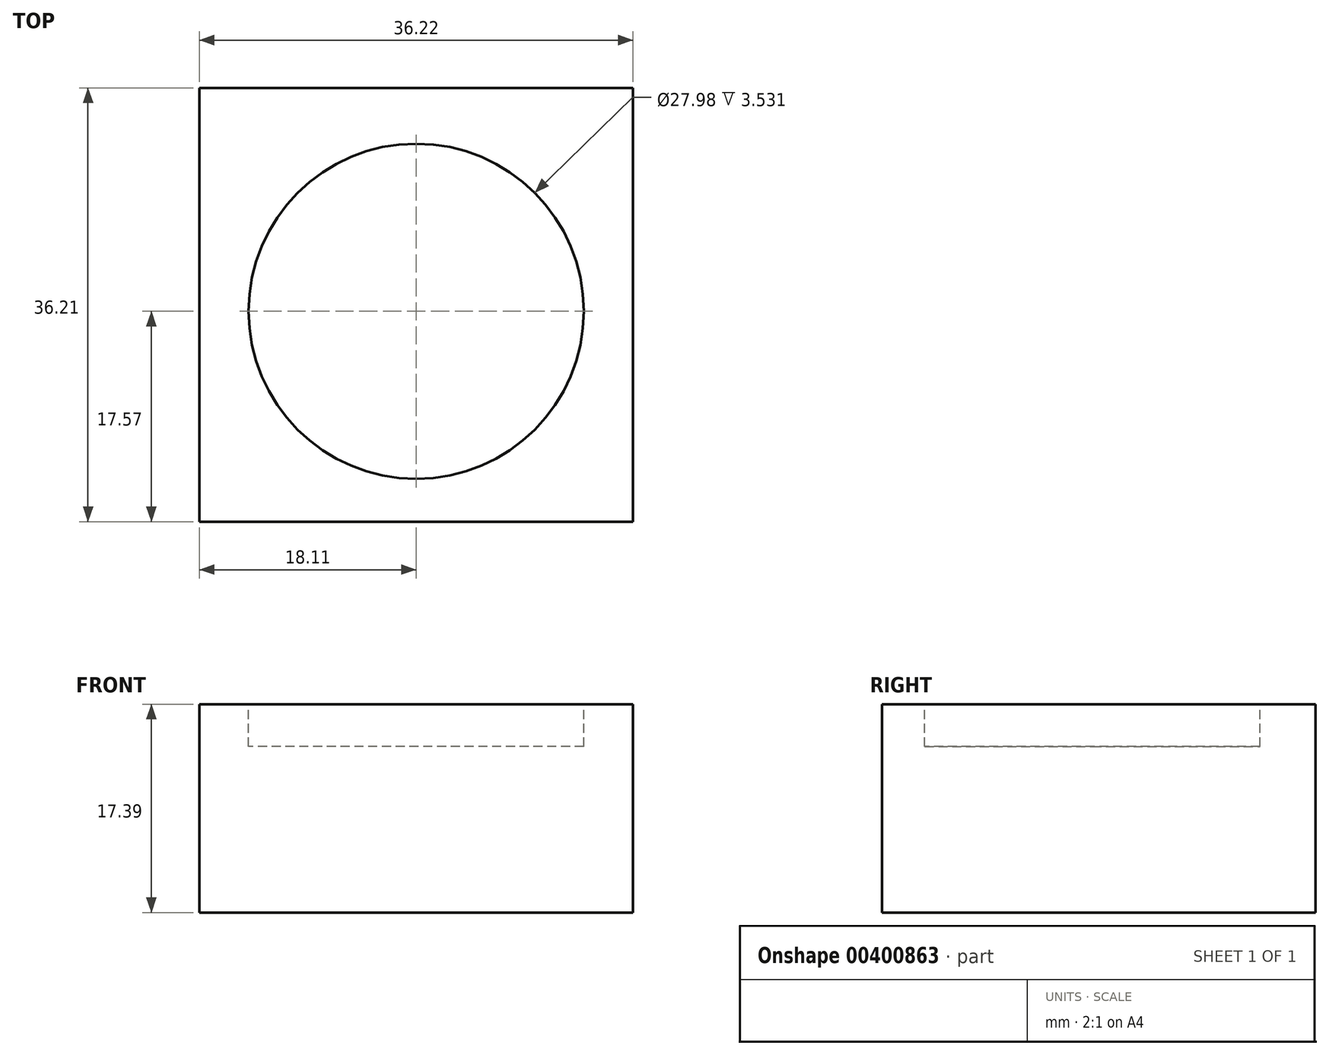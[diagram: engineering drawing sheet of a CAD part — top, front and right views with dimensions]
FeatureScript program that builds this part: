
annotation { "Feature Type Name" : "Feature", "Feature Type Description" : "" }
export const myFeature = defineFeature(function(context is Context, id is Id, definition is map)
    precondition{}
    {
        {
            var Q0;
            Q0=qCreatedBy(makeId("Top.planeOp"),FACE);
            var sketch = newSketch(context, id + "F0", { "sketchPlane" : qUnion([Q0])});
            skLineSegment(sketch, "E0.bottom", {"start": v(18.11, 17.57) * mm, "end": v(-18.11, 17.57) * mm});
            skLineSegment(sketch, "E0.top", {"start": v(18.11, -17.57) * mm, "end": v(-18.11, -17.57) * mm});
            skLineSegment(sketch, "E0.left", {"start": v(18.11, 17.57) * mm, "end": v(18.11, -17.57) * mm});
            skLineSegment(sketch, "E0.right", {"start": v(-18.11, 17.57) * mm, "end": v(-18.11, -17.57) * mm});
            skPoint(sketch, "E0.middle", {"position": v(0, 0) * mm});
            skSolve(sketch);
        }
        {
            var Q0;
            Q0=makeQuery(id+"F0.imprint","IMPRINT",FACE,{"disambiguationData":[TD([[makeQuery(id+"F0.imprint","IMPRINT",EDGE,{"derivedFrom":sQuery(id+"F0.wireOp",EDGE,"E0.bottom")}),1.0]])]});
            var sketch = newSketch(context, id + "F1", { "sketchPlane" : qUnion([Q0])});
            skCircle(sketch, "E1", {"center": v(0, 0) * mm, "radius": 14 * mm});
            skSolve(sketch);
        }
        {
            var Q0;
            Q0=makeQuery(id+"F1.imprint","IMPRINT",FACE,{"disambiguationData":[TD([[makeQuery(id+"F1.imprint","IMPRINT",EDGE,{"derivedFrom":sQuery(id+"F1.wireOp",EDGE,"E1")}),1.0]])]});
            extrude(context, id + "F2", {"entities" : qUnion([Q0]), "depth" : 25.4 * mm});
        }
        {
            var Q0;
            Q0=sQuery(id+"F0.wireOp",EDGE,"E0.top");
            extrude(context, id + "F3", {"bodyType" : ToolBodyType.SURFACE, "surfaceEntities" : qUnion([Q0]), "depth" : 17.4 * mm});
        }
        {
            var Q0;
            Q0=makeQuery(id+"F3.opExtrude","SWEPT_FACE",FACE,{"disambiguationData":[OSD([sQuery(id+"F0.wireOp",EDGE,"E0.top")])]});
            var sketch = newSketch(context, id + "F4", { "sketchPlane" : qUnion([Q0])});
            skSolve(sketch);
        }
        {
            var Q0;
            Q0=makeQuery(id+"F4.imprint","IMPRINT",FACE,{"disambiguationData":[TD([[makeQuery(id+"F4.imprint","IMPRINT",EDGE,{"derivedFrom":makeQuery(id+"F3.opExtrude","SWEPT_EDGE",EDGE,{"disambiguationData":[OSD([sQuery(id+"F0.wireOp",VERTEX,"E0.top.start")])]})}),-1.0]])]});
            extrude(context, id + "F5", {"entities" : qUnion([Q0]), "operationType" : NewBodyOperationType.ADD, "depth" : 36.22 * mm});
        }
        {
            var Q0;
            Q0=makeQuery(id+"F2.opExtrude","CAP_FACE",FACE,{"disambiguationData":[OSD([sQuery(id+"F1.wireOp",EDGE,"E1")])],"isStart":false});
            extrude(context, id + "F6", {"entities" : qUnion([Q0]), "operationType" : NewBodyOperationType.REMOVE, "oppositeDirection" : true, "depth" : 11.54 * mm});
        }
    });
